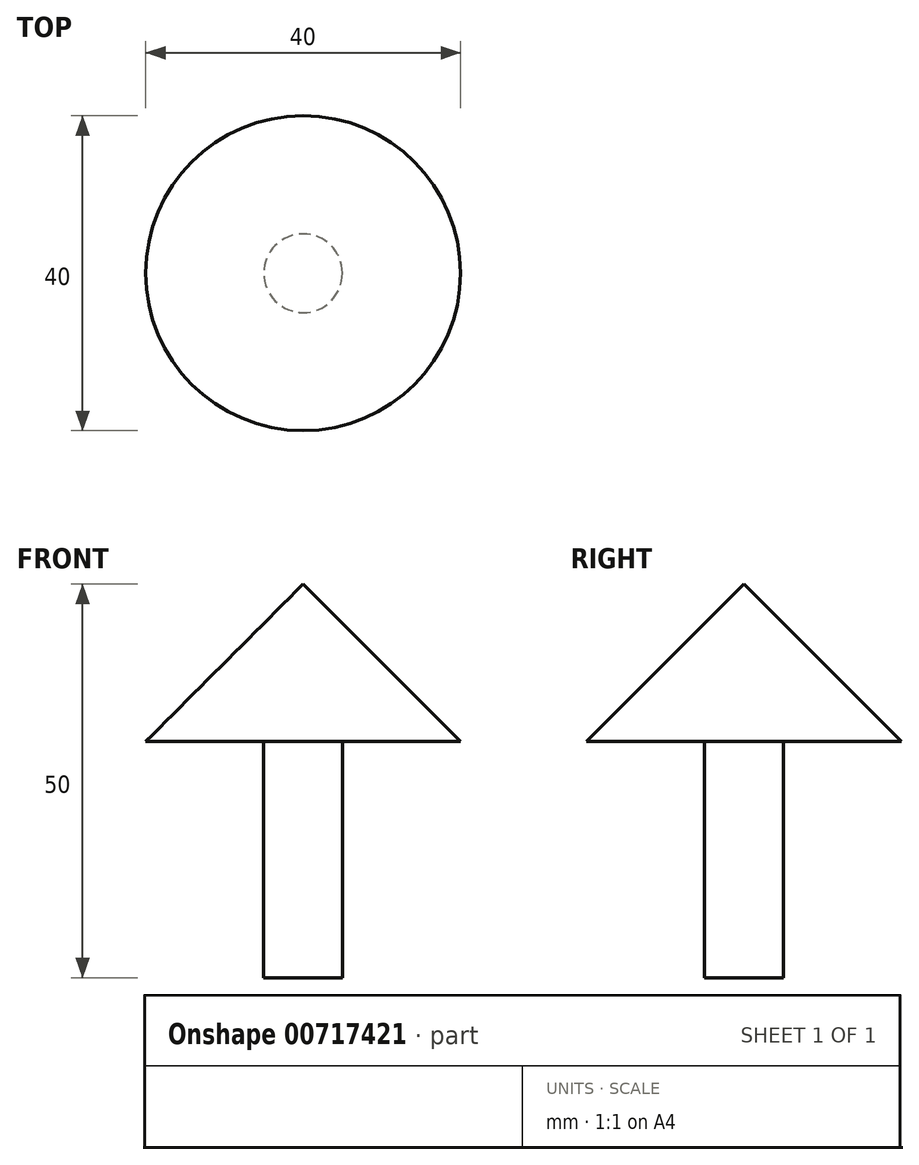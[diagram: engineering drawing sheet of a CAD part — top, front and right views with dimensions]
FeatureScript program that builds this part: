
annotation { "Feature Type Name" : "Feature", "Feature Type Description" : "" }
export const myFeature = defineFeature(function(context is Context, id is Id, definition is map)
    precondition{}
    {
        {
            var Q0;
            Q0=qCreatedBy(makeId("Front.planeOp"),FACE);
            var sketch = newSketch(context, id + "F0", { "sketchPlane" : qUnion([Q0])});
            skLineSegment(sketch, "E0", {"start": v(-15.02, 17.27) * mm, "end": v(-15.02, -32.73) * mm});
            skLineSegment(sketch, "E1", {"start": v(-15.02, -32.73) * mm, "end": v(-10.02, -32.73) * mm});
            skLineSegment(sketch, "E2", {"start": v(-10.02, -32.73) * mm, "end": v(-10.02, -2.73) * mm});
            skLineSegment(sketch, "E3", {"start": v(-10.02, -2.73) * mm, "end": v(4.98, -2.73) * mm});
            skLineSegment(sketch, "E4", {"start": v(4.98, -2.73) * mm, "end": v(-15.02, 17.27) * mm});
            skSolve(sketch);
        }
        {
            var Q0;
            Q0=makeQuery(id+"F0.imprint","IMPRINT",FACE,{"disambiguationData":[TD([[makeQuery(id+"F0.imprint","IMPRINT",EDGE,{"derivedFrom":sQuery(id+"F0.wireOp",EDGE,"E0")}),1.0]])]});
            var Q1;
            Q1=sQuery(id+"F0.wireOp",EDGE,"E0");
            revolve(context, id + "F1", {"surfaceOperationType" : NewSurfaceOperationType.NEW, "entities" : qUnion([Q0]), "axis" : qUnion([Q1]), "revolveType" : RevolveType.FULL});
        }
    });
